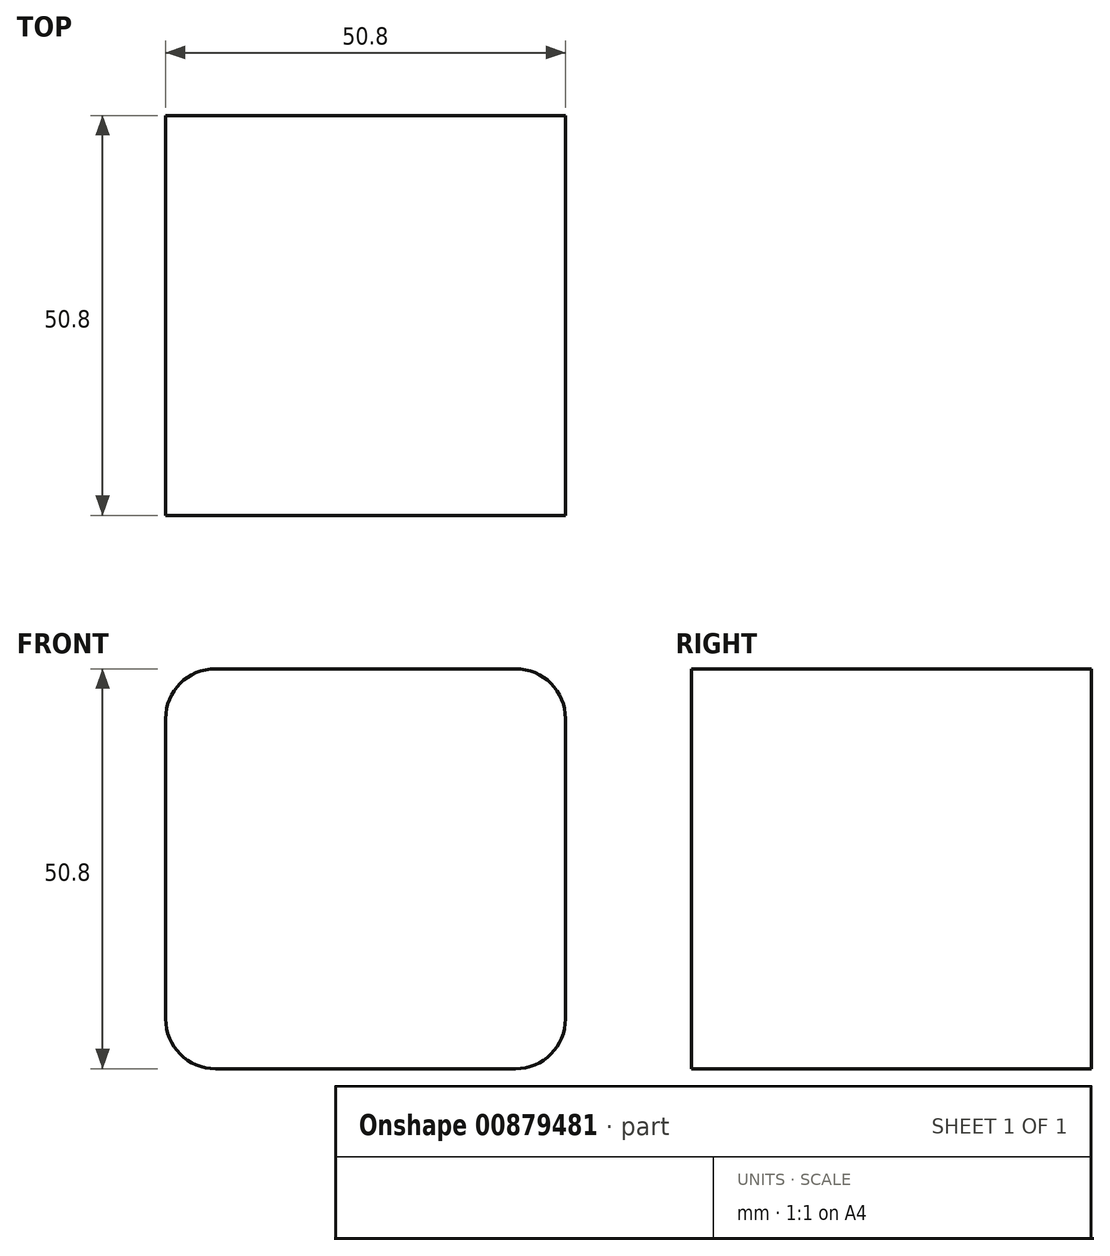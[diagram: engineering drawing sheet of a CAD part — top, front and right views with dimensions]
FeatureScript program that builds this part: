
annotation { "Feature Type Name" : "Feature", "Feature Type Description" : "" }
export const myFeature = defineFeature(function(context is Context, id is Id, definition is map)
    precondition{}
    {
        {
            var Q0;
            Q0=qCreatedBy(makeId("Front.planeOp"),FACE);
            var sketch = newSketch(context, id + "F0", { "sketchPlane" : qUnion([Q0])});
            skLineSegment(sketch, "E0.bottom", {"start": v(19.05, 25.4) * mm, "end": v(-19.05, 25.4) * mm});
            skLineSegment(sketch, "E0.top", {"start": v(19.05, -25.4) * mm, "end": v(-19.05, -25.4) * mm});
            skLineSegment(sketch, "E0.left", {"start": v(25.4, 19.05) * mm, "end": v(25.4, -19.05) * mm});
            skLineSegment(sketch, "E0.right", {"start": v(-25.4, 19.05) * mm, "end": v(-25.4, -19.05) * mm});
            skPoint(sketch, "E0.middle", {"position": v(0, 0) * mm});
            skPoint(sketch, "E1.visualSharp", {"position": v(-25.4, 25.4) * mm});
            skArc(sketch, "E1.filletArc", {"start": v(-19.05, 25.4) * mm, "mid": v(-23.54, 23.54) * mm, "end": v(-25.4, 19.05) * mm});
            skPoint(sketch, "E2.visualSharp", {"position": v(25.4, 25.4) * mm});
            skArc(sketch, "E2.filletArc", {"start": v(25.4, 19.05) * mm, "mid": v(23.54, 23.54) * mm, "end": v(19.05, 25.4) * mm});
            skPoint(sketch, "E3.visualSharp", {"position": v(25.4, -25.4) * mm});
            skArc(sketch, "E3.filletArc", {"start": v(19.05, -25.4) * mm, "mid": v(23.54, -23.54) * mm, "end": v(25.4, -19.05) * mm});
            skPoint(sketch, "E4.visualSharp", {"position": v(-25.4, -25.4) * mm});
            skArc(sketch, "E4.filletArc", {"start": v(-25.4, -19.05) * mm, "mid": v(-23.54, -23.54) * mm, "end": v(-19.05, -25.4) * mm});
            skSolve(sketch);
        }
        {
            var Q0;
            Q0 = qSketchRegion(id + "F0", true);
            extrude(context, id + "F1", {"entities" : qUnion([Q0]), "endBound" : BoundingType.SYMMETRIC, "depth" : 50.8 * mm, "offsetDistance" : 25.4 * mm});
        }
    });
